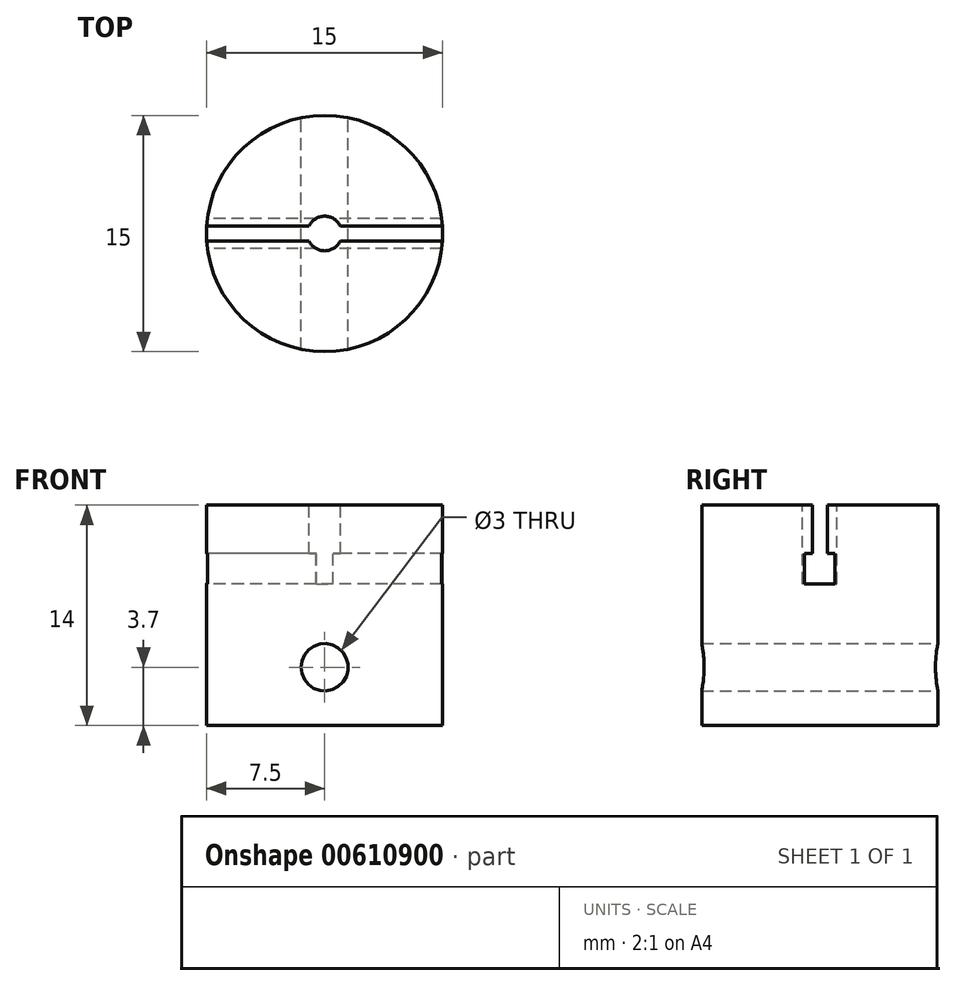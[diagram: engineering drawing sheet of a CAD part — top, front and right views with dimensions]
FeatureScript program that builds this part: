
annotation { "Feature Type Name" : "Feature", "Feature Type Description" : "" }
export const myFeature = defineFeature(function(context is Context, id is Id, definition is map)
    precondition{}
    {
        {
            var Q0;
            Q0=qCreatedBy(makeId("Top.planeOp"),FACE);
            var sketch = newSketch(context, id + "F0", { "sketchPlane" : qUnion([Q0])});
            skCircle(sketch, "E0", {"center": v(0, 0) * mm, "radius": 7.5 * mm});
            skSolve(sketch);
        }
        {
            var Q0;
            Q0=makeQuery(id+"F0.imprint","IMPRINT",FACE,{"disambiguationData":[TD([[makeQuery(id+"F0.imprint","IMPRINT",EDGE,{"derivedFrom":sQuery(id+"F0.wireOp",EDGE,"E0")}),1.0]])]});
            extrude(context, id + "F1", {"entities" : qUnion([Q0]), "depth" : 14 * mm, "offsetDistance" : 25 * mm});
        }
        {
            var Q0;
            Q0=qCreatedBy(makeId("Right.planeOp"),FACE);
            var sketch = newSketch(context, id + "F2", { "sketchPlane" : qUnion([Q0])});
            skLineSegment(sketch, "E1", {"start": v(7.5, 14) * mm, "end": v(7.5, 0) * mm});
            skLineSegment(sketch, "E2", {"start": v(-7.5, 0) * mm, "end": v(-7.5, 14) * mm});
            skSolve(sketch);
        }
        {
            var Q0;
            Q0=sQuery(id+"F2.wireOp",EDGE,"E1");
            cPlane(context, id + "F3", {"entities" : qUnion([Q0]), "cplaneType" : CPlaneType.LINE_ANGLE, "offset" : 25 * mm, "angle" : 90 * degree, "width" : 150 * mm, "height" : 150 * mm});
        }
        {
            var Q0;
            Q0=qCreatedBy(id+"F3.planeOp",FACE);
            var sketch = newSketch(context, id + "F4", { "sketchPlane" : qUnion([Q0])});
            skCircle(sketch, "E3", {"center": v(0, 3.7) * mm, "radius": 1.5 * mm});
            skSolve(sketch);
        }
        {
            var Q0;
            Q0=makeQuery(id+"F4.imprint","IMPRINT",FACE,{"disambiguationData":[TD([[makeQuery(id+"F4.imprint","IMPRINT",EDGE,{"derivedFrom":sQuery(id+"F4.wireOp",EDGE,"E3")}),1.0]])]});
            extrude(context, id + "F5", {"entities" : qUnion([Q0]), "operationType" : NewBodyOperationType.REMOVE, "endBound" : BoundingType.THROUGH_ALL, "oppositeDirection" : true, "depth" : 25 * mm, "offsetDistance" : 25 * mm});
        }
        {
            var Q0;
            Q0=makeQuery(id+"F1.opExtrude","CAP_FACE",FACE,{"disambiguationData":[OSD([sQuery(id+"F0.wireOp",EDGE,"E0")])],"isStart":false});
            var sketch = newSketch(context, id + "F6", { "sketchPlane" : qUnion([Q0])});
            skCircle(sketch, "E4", {"center": v(0, 0) * mm, "radius": 1.1 * mm});
            skSolve(sketch);
        }
        {
            var Q0;
            Q0=makeQuery(id+"F6.imprint","IMPRINT",FACE,{"disambiguationData":[TD([[makeQuery(id+"F6.imprint","IMPRINT",EDGE,{"derivedFrom":sQuery(id+"F6.wireOp",EDGE,"E4")}),1.0]])]});
            extrude(context, id + "F7", {"entities" : qUnion([Q0]), "operationType" : NewBodyOperationType.REMOVE, "oppositeDirection" : true, "depth" : 5 * mm, "offsetDistance" : 25 * mm});
        }
        {
            var Q0;
            Q0=makeQuery(id+"F1.opExtrude","CAP_FACE",FACE,{"disambiguationData":[OSD([sQuery(id+"F0.wireOp",EDGE,"E0")])],"isStart":false});
            var sketch = newSketch(context, id + "F8", { "sketchPlane" : qUnion([Q0])});
            skLineSegment(sketch, "E5.bottom", {"start": v(7.5, -0.47) * mm, "end": v(-7.5, -0.47) * mm});
            skLineSegment(sketch, "E5.top", {"start": v(7.5, 0.47) * mm, "end": v(-7.5, 0.47) * mm});
            skLineSegment(sketch, "E5.left", {"start": v(7.5, -0.47) * mm, "end": v(7.5, 0.47) * mm});
            skLineSegment(sketch, "E5.right", {"start": v(-7.5, -0.47) * mm, "end": v(-7.5, 0.47) * mm});
            skPoint(sketch, "E5.middle", {"position": v(0, 0) * mm});
            skPoint(sketch, "E6", {"position": v(7.5, 0) * mm});
            skSolve(sketch);
        }
        {
            var Q0;
            {var subQ1=makeQuery(id+"F1.opExtrude","CAP_EDGE",EDGE,{"disambiguationData":[OSD([sQuery(id+"F0.wireOp",EDGE,"E0")])],"isStart":false});var subQ6=sQuery(id+"F8.wireOp",EDGE,"E5.bottom");var subQ7=makeQuery(id+"F8.imprint","INTERSECT",VERTEX,{"disambiguationData":[OD(1.0)],"derivedFrom":[subQ1,subQ6]});Q0=makeQuery(id+"F8.imprint","IMPRINT",FACE,{"disambiguationData":[TD([[makeQuery(id+"F8.imprint","IMPRINT",EDGE,{"disambiguationData":[TD([[subQ7,1.0]])],"derivedFrom":subQ6}),-1.0]])]});}
            var Q1;
            {var subQ1=makeQuery(id+"F1.opExtrude","CAP_EDGE",EDGE,{"disambiguationData":[OSD([sQuery(id+"F0.wireOp",EDGE,"E0")])],"isStart":false});var subQ4=sQuery(id+"F8.wireOp",EDGE,"E5.bottom");var subQ5=makeQuery(id+"F8.imprint","INTERSECT",VERTEX,{"disambiguationData":[OD(0.0)],"derivedFrom":[subQ1,subQ4]});Q1=makeQuery(id+"F8.imprint","IMPRINT",FACE,{"disambiguationData":[TD([[makeQuery(id+"F8.imprint","IMPRINT",EDGE,{"disambiguationData":[TD([[subQ5,-1.0]])],"derivedFrom":subQ4}),-1.0]])]});}
            var Q2;
            Q2=makeQuery(id+"F7.boolean.opBoolean","COPY",FACE,{"derivedFrom":makeQuery(id+"F7.opExtrude","CAP_FACE",FACE,{"disambiguationData":[OSD([sQuery(id+"F6.wireOp",EDGE,"E4")])],"isStart":false})});
            extrude(context, id + "F9", {"entities" : qUnion([Q0, Q1]), "operationType" : NewBodyOperationType.REMOVE, "endBound" : BoundingType.UP_TO_SURFACE, "oppositeDirection" : true, "depth" : 25 * mm, "endBoundEntityFace" : qUnion([Q2]), "offsetDistance" : 25 * mm});
        }
        {
            var Q0;
            Q0=qCreatedBy(makeId("Front.planeOp"),FACE);
            var sketch = newSketch(context, id + "F10", { "sketchPlane" : qUnion([Q0])});
            skLineSegment(sketch, "E7", {"start": v(7.5, 9) * mm, "end": v(7.5, 0) * mm});
            skLineSegment(sketch, "E8", {"start": v(-7.5, 0) * mm, "end": v(-7.5, 9) * mm});
            skSolve(sketch);
        }
        {
            var Q0;
            Q0=sQuery(id+"F10.wireOp",EDGE,"E8");
            cPlane(context, id + "F11", {"entities" : qUnion([Q0]), "cplaneType" : CPlaneType.LINE_ANGLE, "offset" : 25 * mm, "angle" : 0 * degree, "width" : 150 * mm, "height" : 150 * mm});
        }
        {
            var Q0;
            Q0=qCreatedBy(id+"F11.planeOp",FACE);
            var sketch = newSketch(context, id + "F12", { "sketchPlane" : qUnion([Q0])});
            skLineSegment(sketch, "E9.0", {"start": v(-0.47, 9) * mm, "end": v(0.47, 9) * mm});
            skLineSegment(sketch, "E10.bottom", {"start": v(0.95, 10.92) * mm, "end": v(-0.97, 10.92) * mm});
            skLineSegment(sketch, "E10.top", {"start": v(0.95, 9) * mm, "end": v(-0.97, 9) * mm});
            skLineSegment(sketch, "E10.left", {"start": v(0.95, 10.92) * mm, "end": v(0.95, 9) * mm});
            skLineSegment(sketch, "E10.right", {"start": v(-0.97, 10.92) * mm, "end": v(-0.97, 9) * mm});
            skSolve(sketch);
        }
        {
            var Q0;
            Q0 = qSketchRegion(id + "F12", true);
            extrude(context, id + "F13", {"entities" : qUnion([Q0]), "operationType" : NewBodyOperationType.REMOVE, "endBound" : BoundingType.THROUGH_ALL, "depth" : 25 * mm, "offsetDistance" : 25 * mm});
        }
    });
